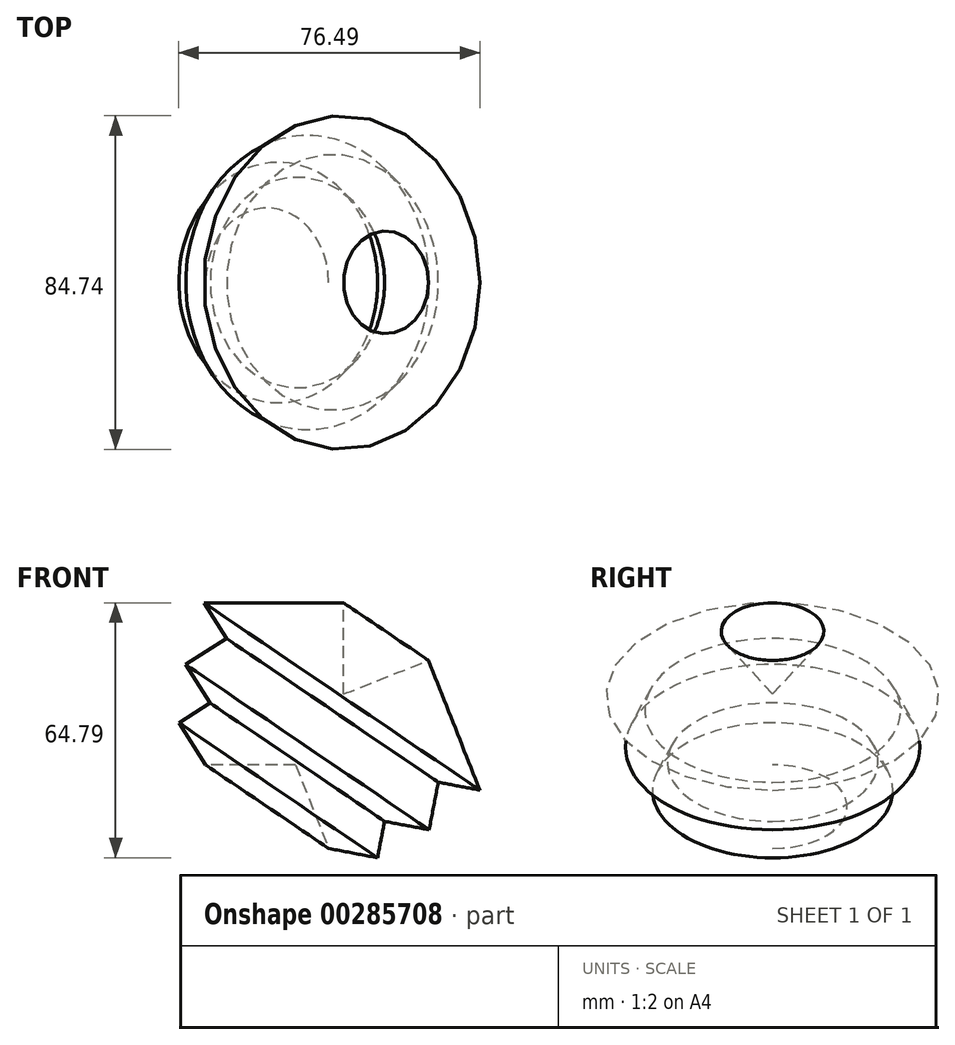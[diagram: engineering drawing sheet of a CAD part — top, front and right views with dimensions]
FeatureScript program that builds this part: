
annotation { "Feature Type Name" : "Feature", "Feature Type Description" : "" }
export const myFeature = defineFeature(function(context is Context, id is Id, definition is map)
    precondition{}
    {
        {
            var Q0;
            Q0=qCreatedBy(makeId("Front.planeOp"),FACE);
            var sketch = newSketch(context, id + "F0", { "sketchPlane" : qUnion([Q0])});
            skLineSegment(sketch, "E0", {"start": v(0, 17.96) * mm, "end": v(-12.2, 0) * mm});
            skLineSegment(sketch, "E1", {"start": v(-12.2, 0) * mm, "end": v(-35.06, 0) * mm});
            skLineSegment(sketch, "E2", {"start": v(-35.06, 0) * mm, "end": v(-41.84, 10.67) * mm});
            skLineSegment(sketch, "E3", {"start": v(-41.84, 10.67) * mm, "end": v(-33.88, 15.73) * mm});
            skLineSegment(sketch, "E4", {"start": v(-33.88, 15.73) * mm, "end": v(-40.07, 25.48) * mm});
            skLineSegment(sketch, "E5", {"start": v(-40.07, 25.48) * mm, "end": v(-29.68, 32.08) * mm});
            skLineSegment(sketch, "E6", {"start": v(-29.68, 32.08) * mm, "end": v(-35.45, 41.17) * mm});
            skLineSegment(sketch, "E7", {"start": v(-35.45, 41.17) * mm, "end": v(0, 41.17) * mm});
            skLineSegment(sketch, "E8", {"start": v(0, 41.17) * mm, "end": v(0, 17.96) * mm});
            skSolve(sketch);
        }
        {
            var Q0;
            Q0=makeQuery(id+"F0.imprint","IMPRINT",FACE,{"disambiguationData":[TD([[makeQuery(id+"F0.imprint","IMPRINT",EDGE,{"derivedFrom":sQuery(id+"F0.wireOp",EDGE,"E0")}),-1.0]])]});
            var Q1;
            Q1=sQuery(id+"F0.wireOp",EDGE,"E0");
            revolve(context, id + "F1", {"entities" : qUnion([Q0]), "axis" : qUnion([Q1]), "revolveType" : RevolveType.FULL});
        }
    });
